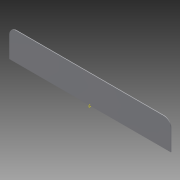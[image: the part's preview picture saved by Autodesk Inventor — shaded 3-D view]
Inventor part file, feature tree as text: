
AUTODESK INVENTOR PART (.ipt)
format: ipt  version: 2013 (Build 170138000, 138)  size: 76,800 bytes
history: native  units: in
note: dims shown in document units (in); Inventor stores cm internally (conversion verified against a paired STEP export)
features: extrude x1, fillet x1, plane x1, sketch x1
ambient origin geometry x8: Origin, YZ Plane, XZ Plane, XY Plane, X Axis, Y Axis, Z Axis, Center Point
bodies: Solid1 (feature_tree)
feature tree (4):
  extrude  "Extrusion1"  Depth=12.0in
  fillet  "Fillet1"  Radius=0.25in
  plane  "Work Plane1"
  sketch  "Sketch1"  dims[d0=69.0in d1=12.0in d2=0.25in d3=0.0in d4=3.0in]
